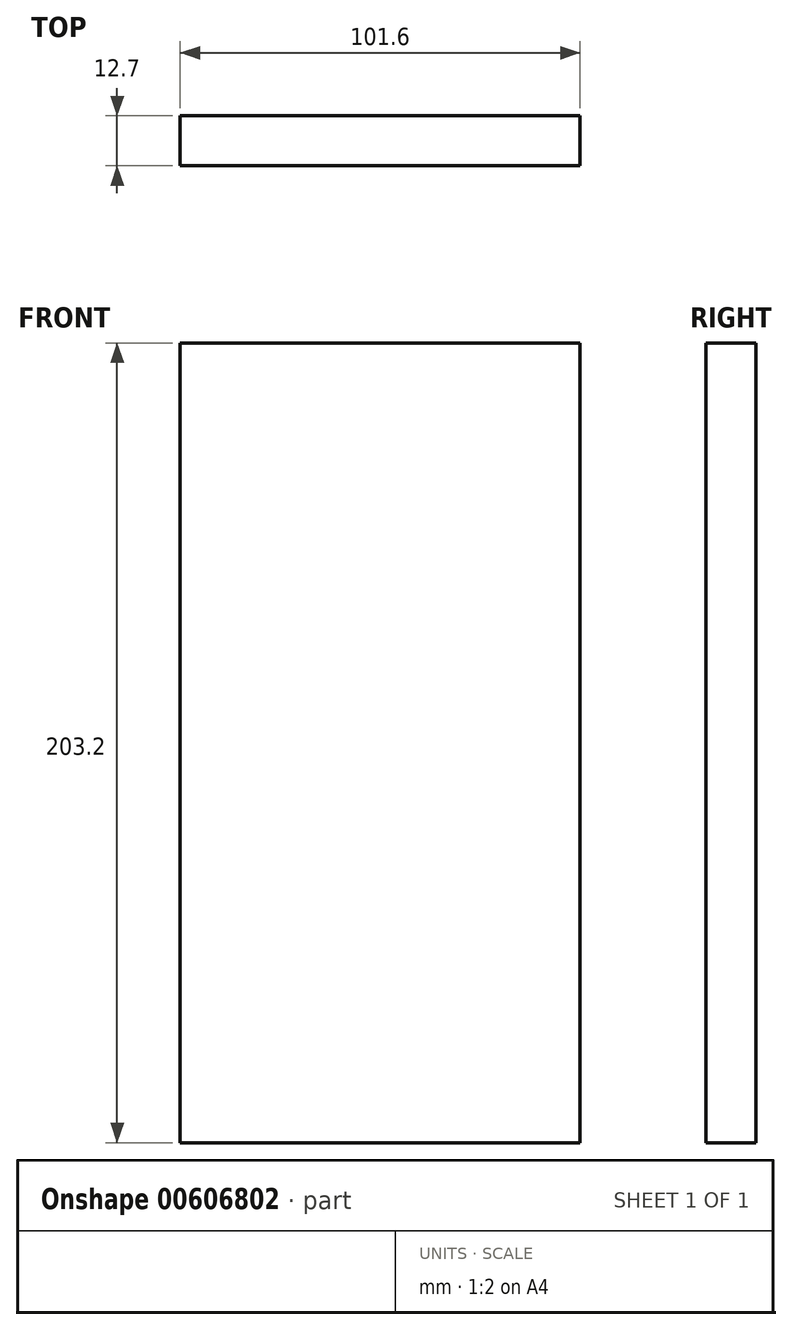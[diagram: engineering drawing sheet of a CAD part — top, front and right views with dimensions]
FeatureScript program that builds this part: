
annotation { "Feature Type Name" : "Feature", "Feature Type Description" : "" }
export const myFeature = defineFeature(function(context is Context, id is Id, definition is map)
    precondition{}
    {
        {
            var Q0;
            Q0=qCreatedBy(makeId("Front.planeOp"),FACE);
            var sketch = newSketch(context, id + "F0", { "sketchPlane" : qUnion([Q0])});
            skLineSegment(sketch, "E0.bottom", {"start": v(-57.4, 148.3) * mm, "end": v(44.2, 148.3) * mm});
            skLineSegment(sketch, "E0.top", {"start": v(-57.4, -54.9) * mm, "end": v(44.2, -54.9) * mm});
            skLineSegment(sketch, "E0.left", {"start": v(-57.4, 148.3) * mm, "end": v(-57.4, -54.9) * mm});
            skLineSegment(sketch, "E0.right", {"start": v(44.2, 148.3) * mm, "end": v(44.2, -54.9) * mm});
            skSolve(sketch);
        }
        {
            var Q0;
            Q0 = qSketchRegion(id + "F0", true);
            extrude(context, id + "F1", {"entities" : qUnion([Q0]), "depth" : 12.7 * mm, "offsetDistance" : 25.4 * mm});
        }
    });
